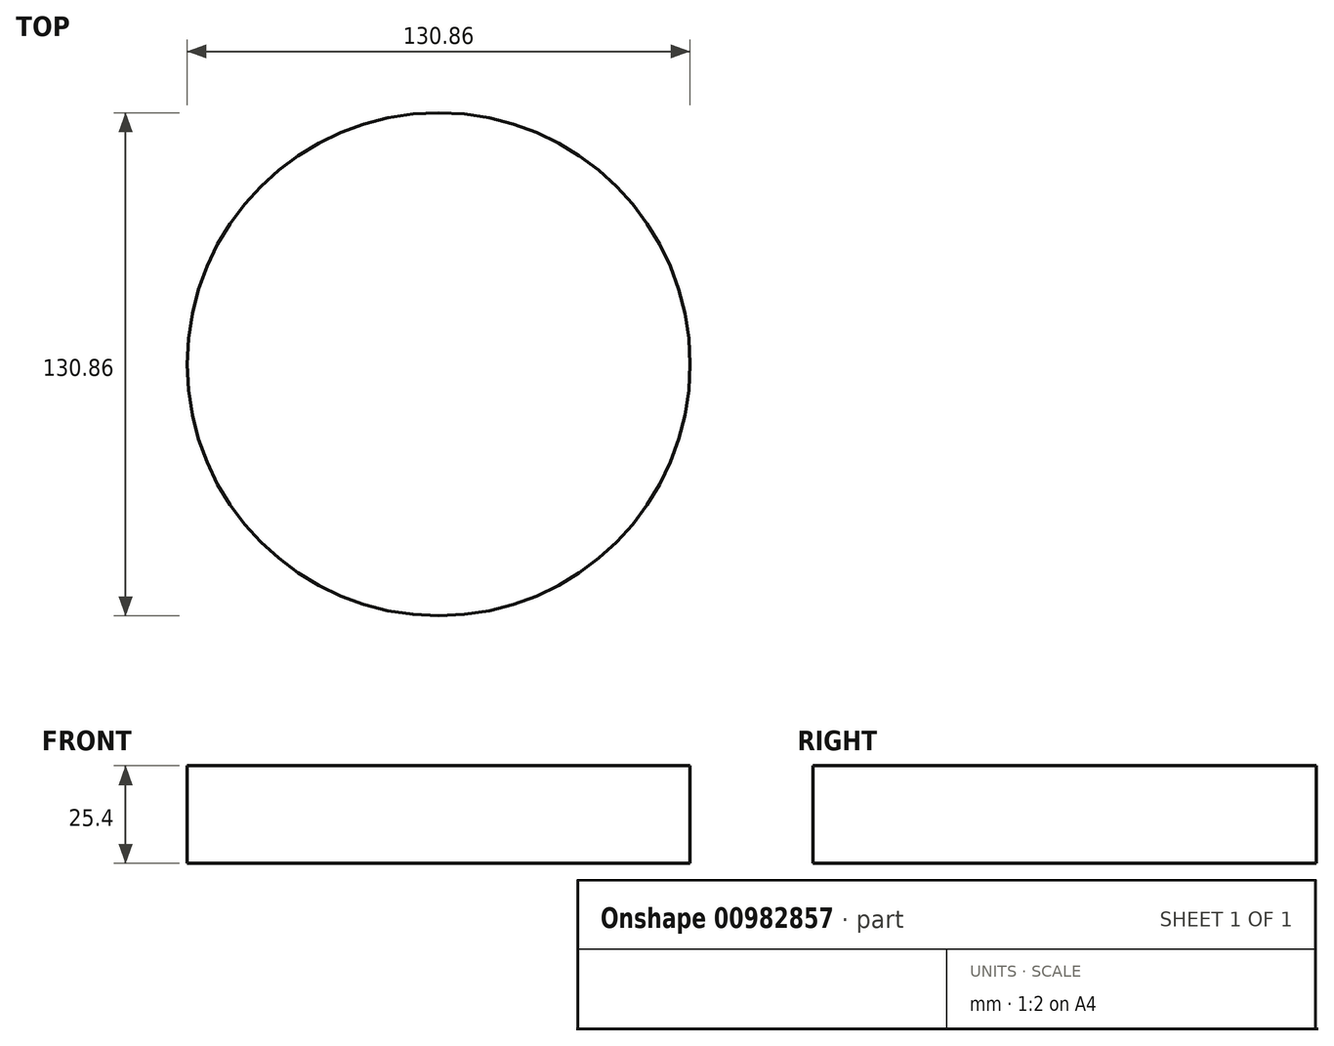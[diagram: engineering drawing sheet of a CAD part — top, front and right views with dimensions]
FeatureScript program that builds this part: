
annotation { "Feature Type Name" : "Feature", "Feature Type Description" : "" }
export const myFeature = defineFeature(function(context is Context, id is Id, definition is map)
    precondition{}
    {
        {
            var Q0;
            Q0=qCreatedBy(makeId("Top.planeOp"),FACE);
            var sketch = newSketch(context, id + "F0", { "sketchPlane" : qUnion([Q0])});
            skCircle(sketch, "E0", {"center": v(0, 0) * mm, "radius": 65.43 * mm});
            skSolve(sketch);
        }
        {
            var Q0;
            Q0=makeQuery(id+"F0.imprint","IMPRINT",FACE,{"disambiguationData":[TD([[makeQuery(id+"F0.imprint","IMPRINT",EDGE,{"derivedFrom":sQuery(id+"F0.wireOp",EDGE,"E0")}),1.0]])]});
            extrude(context, id + "F1", {"entities" : qUnion([Q0]), "endBound" : BoundingType.SYMMETRIC, "depth" : 25.4 * mm, "offsetDistance" : 25.4 * mm});
        }
    });
